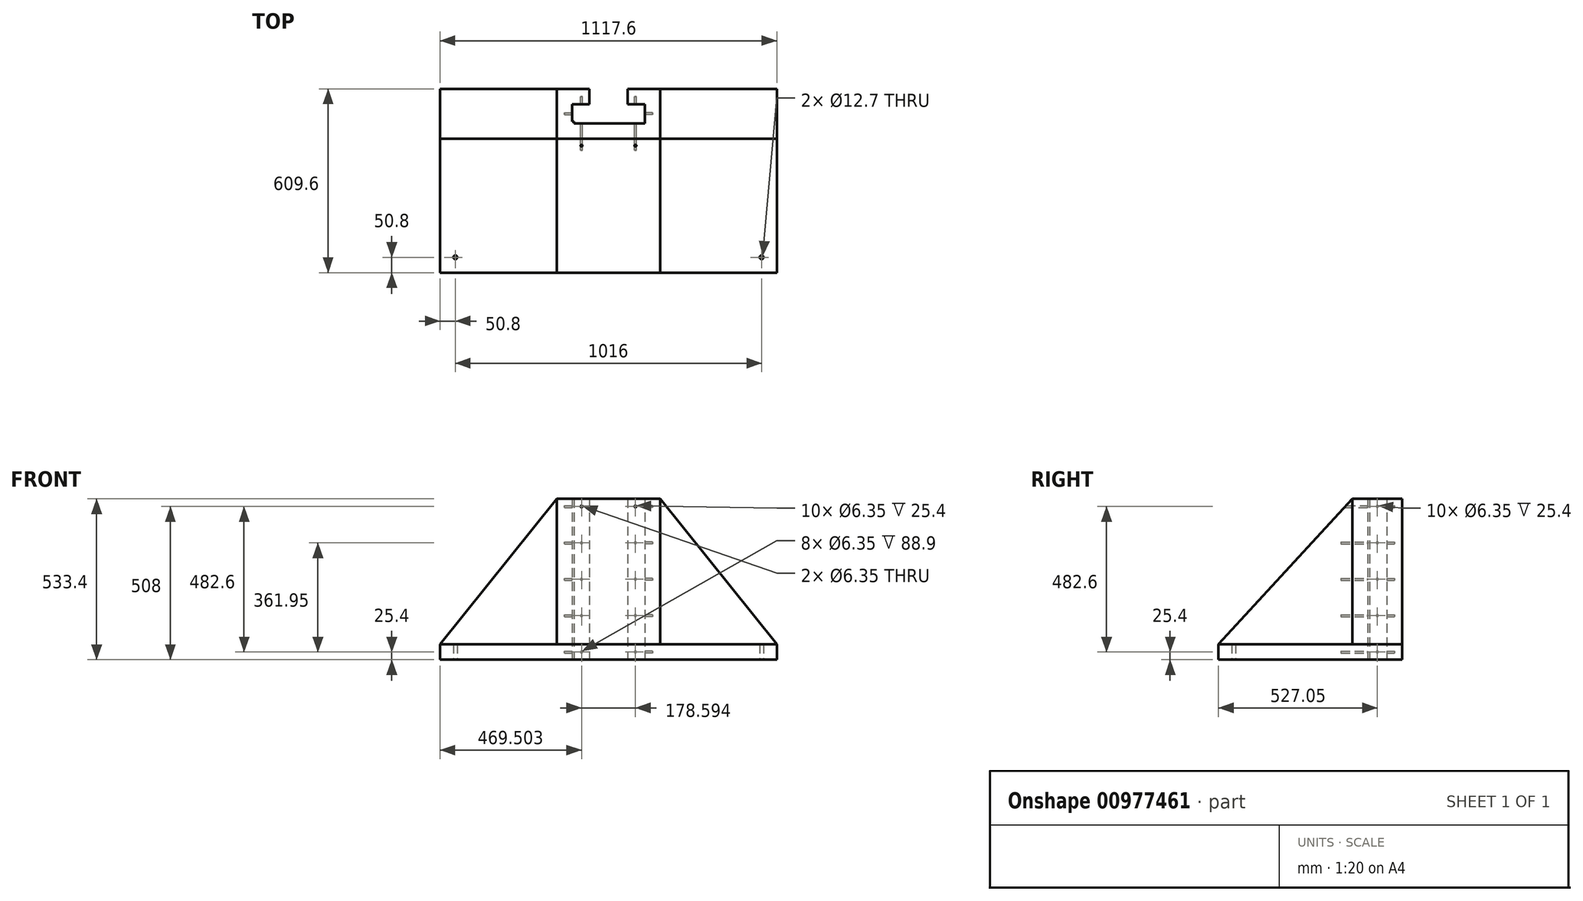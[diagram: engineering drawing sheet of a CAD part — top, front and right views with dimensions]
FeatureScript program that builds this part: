
annotation { "Feature Type Name" : "Feature", "Feature Type Description" : "" }
export const myFeature = defineFeature(function(context is Context, id is Id, definition is map)
    precondition{}
    {
        {
            var Q0;
            Q0=qCreatedBy(makeId("Top.planeOp"),FACE);
            var sketch = newSketch(context, id + "F0", { "sketchPlane" : qUnion([Q0])});
            skLineSegment(sketch, "E0", {"start": v(-171.45, 0) * mm, "end": v(171.45, 0) * mm});
            skLineSegment(sketch, "E1", {"start": v(171.45, 0) * mm, "end": v(171.45, 165.1) * mm});
            skLineSegment(sketch, "E2", {"start": v(171.45, 165.1) * mm, "end": v(63.5, 165.1) * mm});
            skLineSegment(sketch, "E3", {"start": v(63.5, 165.1) * mm, "end": v(63.5, 114.3) * mm});
            skLineSegment(sketch, "E4", {"start": v(63.5, 114.3) * mm, "end": v(120.65, 114.3) * mm});
            skLineSegment(sketch, "E5", {"start": v(120.65, 114.3) * mm, "end": v(120.65, 50.8) * mm});
            skLineSegment(sketch, "E6", {"start": v(120.65, 50.8) * mm, "end": v(-120.65, 50.8) * mm});
            skLineSegment(sketch, "E7", {"start": v(-120.65, 50.8) * mm, "end": v(-120.65, 114.3) * mm});
            skLineSegment(sketch, "E8", {"start": v(-120.65, 114.3) * mm, "end": v(-63.5, 114.3) * mm});
            skLineSegment(sketch, "E9", {"start": v(-63.5, 114.3) * mm, "end": v(-63.5, 165.1) * mm});
            skLineSegment(sketch, "E10", {"start": v(-63.5, 165.1) * mm, "end": v(-171.45, 165.1) * mm});
            skLineSegment(sketch, "E11", {"start": v(-171.45, 165.1) * mm, "end": v(-171.45, 0) * mm});
            skPoint(sketch, "E12", {"position": v(0, 50.8) * mm});
            skLineSegment(sketch, "E13", {"start": v(-171.45, 165.1) * mm, "end": v(-558.8, 165.1) * mm});
            skLineSegment(sketch, "E14", {"start": v(-558.8, 165.1) * mm, "end": v(-558.8, -444.5) * mm});
            skLineSegment(sketch, "E15", {"start": v(-558.8, -444.5) * mm, "end": v(558.8, -444.5) * mm});
            skLineSegment(sketch, "E16", {"start": v(558.8, -444.5) * mm, "end": v(558.8, 165.1) * mm});
            skLineSegment(sketch, "E17", {"start": v(558.8, 165.1) * mm, "end": v(171.45, 165.1) * mm});
            skPoint(sketch, "E18", {"position": v(0, -444.5) * mm});
            skCircle(sketch, "E19", {"center": v(-508, -393.7) * mm, "radius": 6.35 * mm});
            skCircle(sketch, "E20", {"center": v(508, -393.7) * mm, "radius": 6.35 * mm});
            skSolve(sketch);
        }
        {
            var Q0;
            Q0=makeQuery(id+"F0.imprint","IMPRINT",FACE,{"disambiguationData":[TD([[makeQuery(id+"F0.imprint","IMPRINT",EDGE,{"derivedFrom":sQuery(id+"F0.wireOp",EDGE,"E0")}),1.0]])]});
            var Q1;
            Q1 = qSketchRegion(id + "F7", true);
            extrude(context, id + "F1", {"entities" : qUnion([Q0, Q1]), "depth" : 533.4 * mm, "offsetDistance" : 25.4 * mm});
        }
        {
            var Q0;
            Q0 = qSketchRegion(id + "F0", true);
            extrude(context, id + "F2", {"entities" : qUnion([Q0]), "operationType" : NewBodyOperationType.ADD, "depth" : 50.8 * mm, "offsetDistance" : 25.4 * mm});
        }
        {
            var Q0;
            Q0=qCreatedBy(makeId("Right.planeOp"),FACE);
            var sketch = newSketch(context, id + "F3", { "sketchPlane" : qUnion([Q0])});
            skLineSegment(sketch, "E21", {"start": v(0, 50.8) * mm, "end": v(0, 533.4) * mm});
            skLineSegment(sketch, "E22", {"start": v(0, 533.4) * mm, "end": v(-444.5, 50.8) * mm});
            skLineSegment(sketch, "E23", {"start": v(-444.5, 50.8) * mm, "end": v(0, 50.8) * mm});
            skSolve(sketch);
        }
        {
            var Q0;
            Q0 = qSketchRegion(id + "F3", true);
            extrude(context, id + "F4", {"entities" : qUnion([Q0]), "operationType" : NewBodyOperationType.ADD, "endBound" : BoundingType.SYMMETRIC, "depth" : 342.9 * mm, "offsetDistance" : 25.4 * mm});
        }
        {
            var Q0;
            {var subQ0=sQuery(id+"F0.wireOp",EDGE,"E2");Q0=makeQuery(id+"F2.boolean.opBoolean","MERGE",FACE,{"derivedFrom":[makeQuery(id+"F1.opExtrude","SWEPT_FACE",FACE,{"disambiguationData":[OSD([subQ0])]}),makeQuery(id+"F2.opExtrude","SWEPT_FACE",FACE,{"disambiguationData":[OSD([subQ0,sQuery(id+"F0.wireOp",EDGE,"E17")])]})]});}
            var sketch = newSketch(context, id + "F5", { "sketchPlane" : qUnion([Q0])});
            skLineSegment(sketch, "E24", {"start": v(-171.45, 50.8) * mm, "end": v(-558.8, 50.8) * mm});
            skLineSegment(sketch, "E25", {"start": v(-558.8, 50.8) * mm, "end": v(-171.45, 533.4) * mm});
            skLineSegment(sketch, "E26", {"start": v(-171.45, 533.4) * mm, "end": v(-171.45, 50.8) * mm});
            skLineSegment(sketch, "E27.MirrorCS", {"start": v(171.45, 50.8) * mm, "end": v(558.8, 50.8) * mm});
            skLineSegment(sketch, "E28.MirrorCS", {"start": v(171.45, 533.4) * mm, "end": v(171.45, 50.8) * mm});
            skLineSegment(sketch, "E29.MirrorCS", {"start": v(558.8, 50.8) * mm, "end": v(171.45, 533.4) * mm});
            skSolve(sketch);
        }
        {
            var Q0;
            Q0 = qSketchRegion(id + "F5", true);
            extrude(context, id + "F6", {"entities" : qUnion([Q0]), "operationType" : NewBodyOperationType.ADD, "depth" : -165.1 * mm, "offsetDistance" : 25.4 * mm});
        }
        {
            var Q0;
            Q0=makeQuery(id+"F1.opExtrude","SWEPT_FACE",FACE,{"disambiguationData":[OSD([sQuery(id+"F0.wireOp",EDGE,"E6")])]});
            var sketch = newSketch(context, id + "F7", { "sketchPlane" : qUnion([Q0])});
            skCircle(sketch, "E30", {"center": v(-89.3, 146.05) * mm, "radius": 3.18 * mm});
            skCircle(sketch, "E31", {"center": v(-89.3, 266.7) * mm, "radius": 3.18 * mm});
            skCircle(sketch, "E32", {"center": v(-89.3, 25.4) * mm, "radius": 3.18 * mm});
            skCircle(sketch, "E33", {"center": v(-89.3, 508) * mm, "radius": 3.17 * mm});
            skCircle(sketch, "E34", {"center": v(-89.3, 387.35) * mm, "radius": 3.18 * mm});
            skCircle(sketch, "E35.MirrorC", {"center": v(89.3, 25.4) * mm, "radius": 3.18 * mm});
            skCircle(sketch, "E36.MirrorC", {"center": v(89.3, 146.05) * mm, "radius": 3.18 * mm});
            skCircle(sketch, "E37.MirrorC", {"center": v(89.3, 266.7) * mm, "radius": 3.18 * mm});
            skCircle(sketch, "E38.MirrorC", {"center": v(89.3, 387.35) * mm, "radius": 3.18 * mm});
            skCircle(sketch, "E39.MirrorC", {"center": v(89.3, 508) * mm, "radius": 3.17 * mm});
            skSolve(sketch);
        }
        {
            var Q0;
            Q0 = qSketchRegion(id + "F7", true);
            extrude(context, id + "F8", {"entities" : qUnion([Q0]), "operationType" : NewBodyOperationType.REMOVE, "endBound" : BoundingType.SYMMETRIC, "oppositeDirection" : true, "depth" : 177.8 * mm, "offsetDistance" : 25.4 * mm});
        }
        {
            var Q0;
            Q0=makeQuery(id+"F1.opExtrude","SWEPT_FACE",FACE,{"disambiguationData":[OSD([sQuery(id+"F0.wireOp",EDGE,"E5")])]});
            var sketch = newSketch(context, id + "F9", { "sketchPlane" : qUnion([Q0])});
            skCircle(sketch, "E40", {"center": v(-82.55, 25.4) * mm, "radius": 3.18 * mm});
            skCircle(sketch, "E41", {"center": v(-82.55, 146.05) * mm, "radius": 3.18 * mm});
            skCircle(sketch, "E42", {"center": v(-82.55, 266.7) * mm, "radius": 3.18 * mm});
            skCircle(sketch, "E43", {"center": v(-82.55, 387.35) * mm, "radius": 3.18 * mm});
            skCircle(sketch, "E44", {"center": v(-82.55, 508) * mm, "radius": 3.18 * mm});
            skSolve(sketch);
        }
        {
            var Q0;
            Q0 = qSketchRegion(id + "F9", true);
            extrude(context, id + "F10", {"entities" : qUnion([Q0]), "operationType" : NewBodyOperationType.REMOVE, "oppositeDirection" : true, "depth" : 25.4 * mm, "offsetDistance" : 25.4 * mm});
        }
        {
            var Q0;
            Q0=makeQuery(id+"F1.opExtrude","SWEPT_FACE",FACE,{"disambiguationData":[OSD([sQuery(id+"F0.wireOp",EDGE,"E7")])]});
            var sketch = newSketch(context, id + "F11", { "sketchPlane" : qUnion([Q0])});
            skCircle(sketch, "E45", {"center": v(82.55, 25.4) * mm, "radius": 3.18 * mm});
            skCircle(sketch, "E46", {"center": v(82.55, 146.05) * mm, "radius": 3.18 * mm});
            skCircle(sketch, "E47", {"center": v(82.55, 266.7) * mm, "radius": 3.18 * mm});
            skCircle(sketch, "E48", {"center": v(82.55, 387.35) * mm, "radius": 3.18 * mm});
            skCircle(sketch, "E49", {"center": v(82.55, 508) * mm, "radius": 3.18 * mm});
            skSolve(sketch);
        }
        {
            var Q0;
            Q0 = qSketchRegion(id + "F11", true);
            extrude(context, id + "F12", {"entities" : qUnion([Q0]), "operationType" : NewBodyOperationType.REMOVE, "oppositeDirection" : true, "depth" : 25.4 * mm, "offsetDistance" : 25.4 * mm});
        }
        {
            var Q0;
            Q0=qCreatedBy(makeId("Top.planeOp"),FACE);
            var sketch = newSketch(context, id + "F13", { "sketchPlane" : qUnion([Q0])});
            skLineSegment(sketch, "E50", {"start": v(-114.3, 50.8) * mm, "end": v(-114.3, 57.15) * mm});
            skLineSegment(sketch, "E51", {"start": v(-114.3, 57.15) * mm, "end": v(-120.65, 57.15) * mm});
            skLineSegment(sketch, "E52", {"start": v(-120.65, 57.15) * mm, "end": v(-120.65, 50.8) * mm});
            skLineSegment(sketch, "E53", {"start": v(-120.65, 50.8) * mm, "end": v(-114.3, 50.8) * mm});
            skSolve(sketch);
        }
        {
            var Q0;
            Q0 = qSketchRegion(id + "F13", true);
            extrude(context, id + "F14", {"entities" : qUnion([Q0]), "operationType" : NewBodyOperationType.ADD, "depth" : 533.4 * mm, "offsetDistance" : 25.4 * mm});
        }
    });
